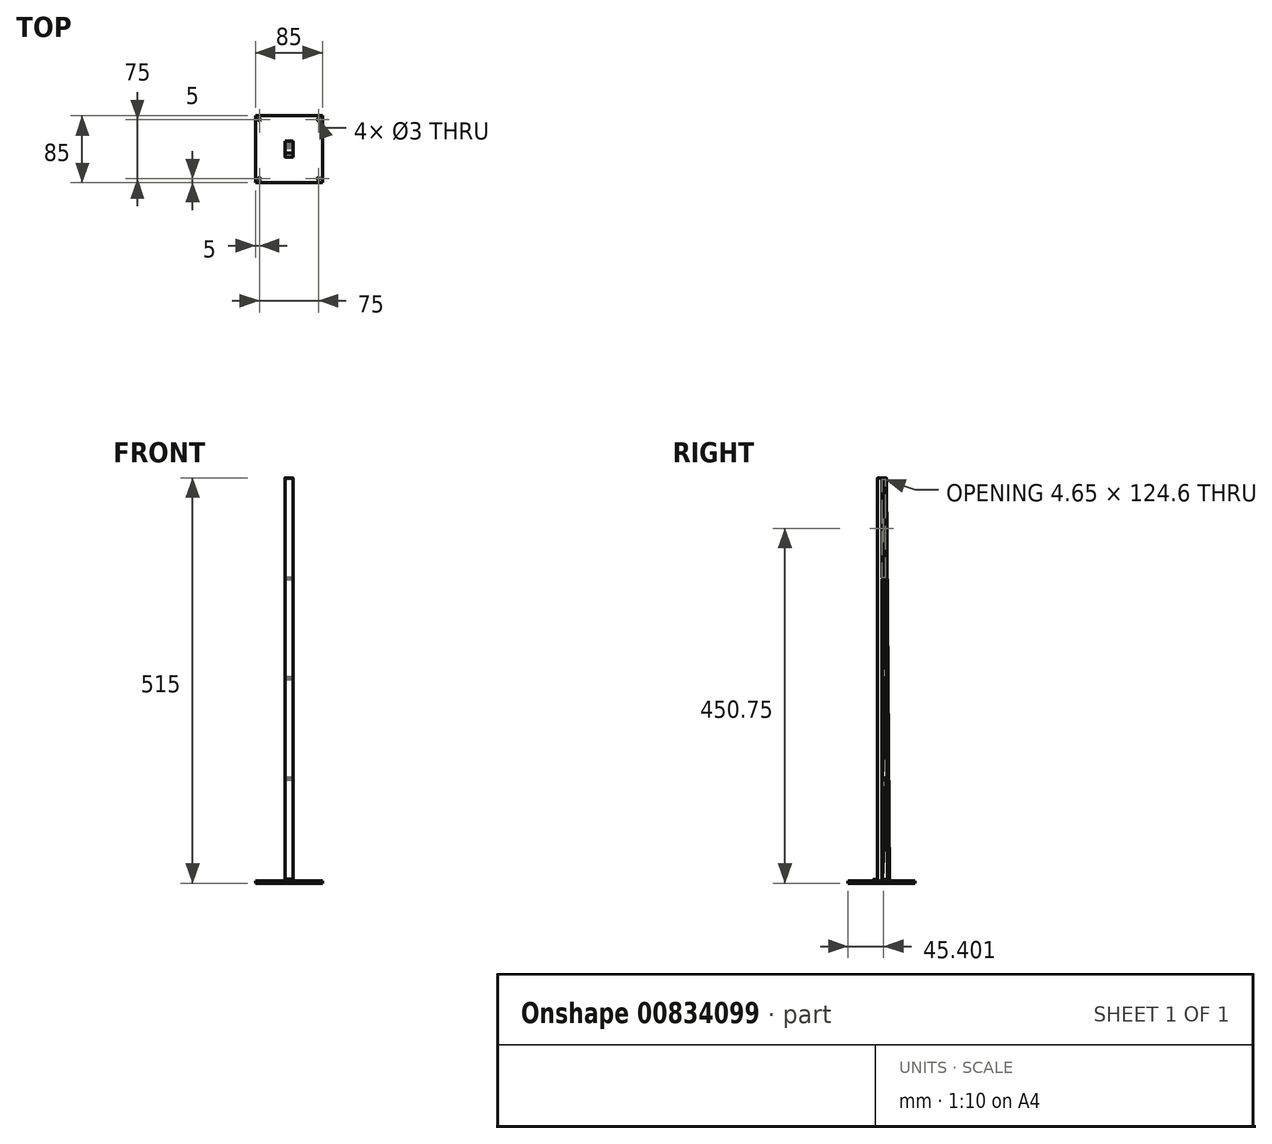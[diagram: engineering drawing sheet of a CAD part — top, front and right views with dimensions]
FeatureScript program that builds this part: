
annotation { "Feature Type Name" : "Feature", "Feature Type Description" : "" }
export const myFeature = defineFeature(function(context is Context, id is Id, definition is map)
    precondition{}
    {
        {
            var Q0;
            Q0=qCreatedBy(makeId("Front.planeOp"),FACE);
            var sketch = newSketch(context, id + "F0", { "sketchPlane" : qUnion([Q0])});
            skLineSegment(sketch, "E0.bottom", {"start": v(5, 255) * mm, "end": v(-5, 255) * mm});
            skLineSegment(sketch, "E0.top", {"start": v(5, -255) * mm, "end": v(-5, -255) * mm});
            skLineSegment(sketch, "E0.left", {"start": v(5, 255) * mm, "end": v(5, -255) * mm});
            skLineSegment(sketch, "E0.right", {"start": v(-5, 255) * mm, "end": v(-5, -255) * mm});
            skPoint(sketch, "E0.middle", {"position": v(0, 0) * mm});
            skSolve(sketch);
        }
        {
            var Q0;
            Q0 = qSketchRegion(id + "F0", true);
            extrude(context, id + "F1", {"entities" : qUnion([Q0]), "depth" : 5 * mm, "offsetDistance" : 25.4 * mm});
        }
        {
            var Q0;
            Q0=makeQuery(id+"F1.opExtrude","SWEPT_FACE",FACE,{"disambiguationData":[OSD([sQuery(id+"F0.wireOp",EDGE,"E0.top")])]});
            var sketch = newSketch(context, id + "F2", { "sketchPlane" : qUnion([Q0])});
            skLineSegment(sketch, "E1.bottom", {"start": v(-5, 10) * mm, "end": v(5, 10) * mm});
            skLineSegment(sketch, "E1.top", {"start": v(-5, -10) * mm, "end": v(5, -10) * mm});
            skLineSegment(sketch, "E1.left", {"start": v(-5, 10) * mm, "end": v(-5, -10) * mm});
            skLineSegment(sketch, "E1.right", {"start": v(5, 10) * mm, "end": v(5, -10) * mm});
            skPoint(sketch, "E1.middle", {"position": v(0, 0) * mm});
            skSolve(sketch);
        }
        {
            var Q0;
            Q0 = qSketchRegion(id + "F2", true);
            extrude(context, id + "F3", {"entities" : qUnion([Q0]), "operationType" : NewBodyOperationType.ADD, "depth" : 2 * mm, "offsetDistance" : 25 * mm});
        }
        {
            var Q0;
            Q0=makeQuery(id+"F1.opExtrude","CAP_FACE",FACE,{"disambiguationData":[OSD([sQuery(id+"F0.wireOp",EDGE,"E0.bottom"),sQuery(id+"F0.wireOp",EDGE,"E0.top"),sQuery(id+"F0.wireOp",EDGE,"E0.left"),sQuery(id+"F0.wireOp",EDGE,"E0.right")])],"isStart":true});
            var sketch = newSketch(context, id + "F4", { "sketchPlane" : qUnion([Q0])});
            skLineSegment(sketch, "E2.bottom", {"start": v(5, -255) * mm, "end": v(-5, -255) * mm});
            skLineSegment(sketch, "E2.top", {"start": v(5, 255) * mm, "end": v(-5, 255) * mm});
            skLineSegment(sketch, "E2.left", {"start": v(5, -255) * mm, "end": v(5, 255) * mm});
            skLineSegment(sketch, "E2.right", {"start": v(-5, -255) * mm, "end": v(-5, 255) * mm});
            skPoint(sketch, "E2.middle", {"position": v(0, 0) * mm});
            skSolve(sketch);
        }
        {
            var Q0;
            Q0=makeQuery(id+"F4.imprint","IMPRINT",FACE,{"disambiguationData":[TD([[makeQuery(id+"F4.imprint","IMPRINT",EDGE,{"derivedFrom":sQuery(id+"F4.wireOp",EDGE,"E2.bottom")}),1.0]])]});
            extrude(context, id + "F5", {"entities" : qUnion([Q0]), "operationType" : NewBodyOperationType.ADD, "depth" : 10 * mm, "offsetDistance" : 25 * mm});
        }
        {
            var Q0;
            Q0=makeQuery(id+"F5.boolean.opBoolean","MERGE",FACE,{"derivedFrom":[makeQuery(id+"F3.boolean.opBoolean","MERGE",FACE,{"derivedFrom":[makeQuery(id+"F1.opExtrude","SWEPT_FACE",FACE,{"disambiguationData":[OSD([sQuery(id+"F0.wireOp",EDGE,"E0.right")])]}),makeQuery(id+"F3.opExtrude","SWEPT_FACE",FACE,{"disambiguationData":[OSD([sQuery(id+"F2.wireOp",EDGE,"E1.left")])]})]}),makeQuery(id+"F5.opExtrude","SWEPT_FACE",FACE,{"disambiguationData":[OSD([sQuery(id+"F4.wireOp",EDGE,"E2.left")])]})]});
            var sketch = newSketch(context, id + "F6", { "sketchPlane" : qUnion([Q0])});
            skLineSegment(sketch, "E3", {"start": v(0, -257) * mm, "end": v(-2.5, 255) * mm});
            skPoint(sketch, "E4", {"position": v(-6.25, 255) * mm});
            skPoint(sketch, "E5", {"position": v(-2.5, 253) * mm});
            skLineSegment(sketch, "E6", {"start": v(-6.25, 255) * mm, "end": v(-10, -257) * mm});
            skSolve(sketch);
        }
        {
            var Q0;
            {var subQ0=sQuery(id+"F6.wireOp",EDGE,"E6");Q0=makeQuery(id+"F6.imprint","IMPRINT",FACE,{"disambiguationData":[TD([[makeQuery(id+"F6.imprint","IMPRINT",EDGE,{"derivedFrom":subQ0}),-1.0]])]});}
            extrude(context, id + "F7", {"entities" : qUnion([Q0]), "operationType" : NewBodyOperationType.REMOVE, "oppositeDirection" : true, "depth" : 25 * mm, "offsetDistance" : 25 * mm});
        }
        {
            var Q0;
            Q0=makeQuery(id+"F5.boolean.opBoolean","MERGE",FACE,{"derivedFrom":[makeQuery(id+"F3.boolean.opBoolean","MERGE",FACE,{"derivedFrom":[makeQuery(id+"F1.opExtrude","SWEPT_FACE",FACE,{"disambiguationData":[OSD([sQuery(id+"F0.wireOp",EDGE,"E0.right")])]}),makeQuery(id+"F3.opExtrude","SWEPT_FACE",FACE,{"disambiguationData":[OSD([sQuery(id+"F2.wireOp",EDGE,"E1.left")])]})]}),makeQuery(id+"F5.opExtrude","SWEPT_FACE",FACE,{"disambiguationData":[OSD([sQuery(id+"F4.wireOp",EDGE,"E2.left")])]})]});
            var sketch = newSketch(context, id + "F8", { "sketchPlane" : qUnion([Q0])});
            skLineSegment(sketch, "E7", {"start": v(-0.62, 255) * mm, "end": v(-0.62, -257) * mm});
            skPoint(sketch, "E8", {"position": v(-0.62, 253) * mm});
            skPoint(sketch, "E9", {"position": v(-0.62, 127.5) * mm});
            skPoint(sketch, "E10", {"position": v(-0.62, 128.5) * mm});
            skPoint(sketch, "E11", {"position": v(-0.62, 126.5) * mm});
            skPoint(sketch, "E12", {"position": v(-0.62, 0) * mm});
            skPoint(sketch, "E13", {"position": v(-0.62, 1) * mm});
            skPoint(sketch, "E14", {"position": v(-0.62, -1) * mm});
            skPoint(sketch, "E15", {"position": v(-0.62, -127.5) * mm});
            skPoint(sketch, "E16", {"position": v(-0.62, -126.5) * mm});
            skPoint(sketch, "E17", {"position": v(-0.62, -128.5) * mm});
            skPoint(sketch, "E18", {"position": v(-0.62, -255) * mm});
            skPoint(sketch, "E19", {"position": v(-7.2, 126.5) * mm});
            skPoint(sketch, "E20", {"position": v(-7.2, 128.5) * mm});
            skPoint(sketch, "E21", {"position": v(-5.2, 126.5) * mm});
            skPoint(sketch, "E22", {"position": v(-5.2, 128.5) * mm});
            skPoint(sketch, "E23", {"position": v(-8.12, -1) * mm});
            skPoint(sketch, "E24", {"position": v(-8.12, 1) * mm});
            skPoint(sketch, "E25", {"position": v(-6.25, 1) * mm});
            skPoint(sketch, "E26", {"position": v(-6.25, -1) * mm});
            skPoint(sketch, "E27", {"position": v(-9.04, -126.5) * mm});
            skPoint(sketch, "E28", {"position": v(-9.04, -128.5) * mm});
            skPoint(sketch, "E29", {"position": v(-7.1, -126.5) * mm});
            skPoint(sketch, "E30", {"position": v(-7.1, -128.5) * mm});
            skPoint(sketch, "E31", {"position": v(-9.99, -255) * mm});
            skPoint(sketch, "E32", {"position": v(-7.99, -255) * mm});
            skPoint(sketch, "E33", {"position": v(-6.25, 253) * mm});
            skPoint(sketch, "E34", {"position": v(-4.25, 253) * mm});
            skLineSegment(sketch, "E35", {"start": v(-0.62, 253) * mm, "end": v(-4.25, 253) * mm});
            skLineSegment(sketch, "E36", {"start": v(-4.25, 253) * mm, "end": v(-5.2, 126.5) * mm});
            skLineSegment(sketch, "E37", {"start": v(-5.2, 126.5) * mm, "end": v(-6.25, -1) * mm});
            skLineSegment(sketch, "E38", {"start": v(-6.25, -1) * mm, "end": v(-7.1, -128.5) * mm});
            skLineSegment(sketch, "E39", {"start": v(-7.1, -128.5) * mm, "end": v(-7.99, -255) * mm});
            skLineSegment(sketch, "E40", {"start": v(-7.99, -255) * mm, "end": v(-0.62, -255) * mm});
            skLineSegment(sketch, "E41", {"start": v(-0.62, 128.5) * mm, "end": v(-5.2, 128.5) * mm});
            skLineSegment(sketch, "E42", {"start": v(-0.62, 126.5) * mm, "end": v(-5.2, 126.5) * mm});
            skLineSegment(sketch, "E43", {"start": v(-0.62, 1) * mm, "end": v(-6.25, 1) * mm});
            skLineSegment(sketch, "E44", {"start": v(-0.62, -1) * mm, "end": v(-6.25, -1) * mm});
            skLineSegment(sketch, "E45", {"start": v(-0.62, -126.5) * mm, "end": v(-7.1, -126.5) * mm});
            skLineSegment(sketch, "E46", {"start": v(-0.62, -128.5) * mm, "end": v(-7.1, -128.5) * mm});
            skPoint(sketch, "E47", {"position": v(-4.2, 126.5) * mm});
            skPoint(sketch, "E48", {"position": v(-5.2, 125.5) * mm});
            skPoint(sketch, "E49", {"position": v(-0.62, 2) * mm});
            skPoint(sketch, "E50", {"position": v(-1.62, 1) * mm});
            skPoint(sketch, "E51", {"position": v(-0.62, -125.5) * mm});
            skPoint(sketch, "E52", {"position": v(-1.62, -126.5) * mm});
            skPoint(sketch, "E53", {"position": v(-0.62, -254) * mm});
            skPoint(sketch, "E54", {"position": v(-1.62, -255) * mm});
            skPoint(sketch, "E55", {"position": v(-6.1, -128.5) * mm});
            skPoint(sketch, "E56", {"position": v(-7.1, -129.5) * mm});
            skPoint(sketch, "E57", {"position": v(-5.25, -1) * mm});
            skPoint(sketch, "E58", {"position": v(-6.26, -2) * mm});
            skLineSegment(sketch, "E59", {"start": v(-4.2, 126.5) * mm, "end": v(-0.62, 2) * mm});
            skLineSegment(sketch, "E60", {"start": v(-1.62, 1) * mm, "end": v(-5.2, 125.5) * mm});
            skLineSegment(sketch, "E61", {"start": v(-5.25, -1) * mm, "end": v(-0.62, -125.5) * mm});
            skLineSegment(sketch, "E62", {"start": v(-6.26, -2) * mm, "end": v(-1.62, -126.5) * mm});
            skLineSegment(sketch, "E63", {"start": v(-6.1, -128.5) * mm, "end": v(-0.62, -254) * mm});
            skLineSegment(sketch, "E64", {"start": v(-1.62, -255) * mm, "end": v(-7.1, -129.5) * mm});
            skSolve(sketch);
        }
        {
            var Q0;
            {var subQ3=sQuery(id+"F8.wireOp",EDGE,"E63");Q0=makeQuery(id+"F8.imprint","IMPRINT",FACE,{"disambiguationData":[TD([[makeQuery(id+"F8.imprint","IMPRINT",EDGE,{"derivedFrom":subQ3}),1.0]])]});}
            var Q1;
            {var subQ3=sQuery(id+"F8.wireOp",EDGE,"E64");Q1=makeQuery(id+"F8.imprint","IMPRINT",FACE,{"disambiguationData":[TD([[makeQuery(id+"F8.imprint","IMPRINT",EDGE,{"derivedFrom":subQ3}),1.0]])]});}
            var Q2;
            {var subQ0=sQuery(id+"F8.wireOp",EDGE,"E62");Q2=makeQuery(id+"F8.imprint","IMPRINT",FACE,{"disambiguationData":[TD([[makeQuery(id+"F8.imprint","IMPRINT",EDGE,{"derivedFrom":subQ0}),-1.0]])]});}
            var Q3;
            {var subQ3=sQuery(id+"F8.wireOp",EDGE,"E61");Q3=makeQuery(id+"F8.imprint","IMPRINT",FACE,{"disambiguationData":[TD([[makeQuery(id+"F8.imprint","IMPRINT",EDGE,{"derivedFrom":subQ3}),1.0]])]});}
            var Q4;
            {var subQ0=sQuery(id+"F8.wireOp",EDGE,"E60");Q4=makeQuery(id+"F8.imprint","IMPRINT",FACE,{"disambiguationData":[TD([[makeQuery(id+"F8.imprint","IMPRINT",EDGE,{"derivedFrom":subQ0}),1.0]])]});}
            var Q5;
            {var subQ3=sQuery(id+"F8.wireOp",EDGE,"E59");Q5=makeQuery(id+"F8.imprint","IMPRINT",FACE,{"disambiguationData":[TD([[makeQuery(id+"F8.imprint","IMPRINT",EDGE,{"derivedFrom":subQ3}),1.0]])]});}
            var Q6;
            {var subQ0=sQuery(id+"F8.wireOp",EDGE,"E35");Q6=makeQuery(id+"F8.imprint","IMPRINT",FACE,{"disambiguationData":[TD([[makeQuery(id+"F8.imprint","IMPRINT",EDGE,{"derivedFrom":subQ0}),1.0]])]});}
            extrude(context, id + "F9", {"entities" : qUnion([Q0, Q1, Q2, Q3, Q4, Q5, Q6]), "operationType" : NewBodyOperationType.REMOVE, "oppositeDirection" : true, "depth" : 25 * mm, "offsetDistance" : 25 * mm});
        }
        {
            var Q0;
            {var subQ0=sQuery(id+"F2.wireOp",EDGE,"E1.bottom");var subQ2=sQuery(id+"F2.wireOp",EDGE,"E1.left");var subQ4=sQuery(id+"F2.wireOp",EDGE,"E1.right");Q0=makeQuery(id+"F3.boolean.opBoolean","SPLIT",FACE,{"disambiguationData":[TD([makeQuery(id+"F3.opExtrude","SWEPT_FACE",FACE,{"disambiguationData":[OSD([subQ0])]})])],"derivedFrom":makeQuery(id+"F3.opExtrude","CAP_FACE",FACE,{"disambiguationData":[OSD([subQ0,sQuery(id+"F2.wireOp",EDGE,"E1.top"),subQ2,subQ4])],"isStart":true})});}
            var Q1;
            Q1=makeQuery(id+"F3.opExtrude","CAP_EDGE",EDGE,{"disambiguationData":[OSD([sQuery(id+"F2.wireOp",EDGE,"E1.right")])],"isStart":false});
            var Q2;
            {var subQ0=sQuery(id+"F2.wireOp",EDGE,"E1.top");Q2=makeQuery(id+"F7.boolean.opBoolean","MERGE",EDGE,{"derivedFrom":[makeQuery(id+"F3.opExtrude","CAP_EDGE",EDGE,{"disambiguationData":[OSD([subQ0])],"isStart":false}),makeQuery(id+"F7.opExtrude","SWEPT_EDGE",EDGE,{"disambiguationData":[OSD([subQ0,sQuery(id+"F2.wireOp",EDGE,"E1.left"),sQuery(id+"F4.wireOp",EDGE,"E2.left"),sQuery(id+"F6.wireOp",EDGE,"E6")])]})]});}
            var Q3;
            Q3=makeQuery(id+"F3.opExtrude","CAP_EDGE",EDGE,{"disambiguationData":[OSD([sQuery(id+"F2.wireOp",EDGE,"E1.left")])],"isStart":false});
            var Q4;
            Q4=makeQuery(id+"F3.opExtrude","CAP_EDGE",EDGE,{"disambiguationData":[OSD([sQuery(id+"F2.wireOp",EDGE,"E1.bottom")])],"isStart":false});
            fillet(context, id + "F10", {"entities" : qUnion([Q0, Q1, Q2, Q3, Q4]), "radius" : 0.05 * mm, "tangentPropagation" : true, "allowEdgeOverflow" : false});
        }
        {
            var Q0;
            {var subQ0=sQuery(id+"F8.wireOp",EDGE,"E7");Q0=makeQuery(id+"F9.boolean.opBoolean","COPY",EDGE,{"derivedFrom":makeQuery(id+"F9.opExtrude","CAP_EDGE",EDGE,{"disambiguationData":[OSD([subQ0]),TDD([makeQuery(id+"F8.imprint","IMPRINT",EDGE,{"disambiguationData":[TD([[makeQuery(id+"F8.imprint","INTERSECT",VERTEX,{"derivedFrom":[subQ0,sQuery(id+"F8.wireOp",EDGE,"E35")]}),-1.0]])],"derivedFrom":subQ0})])],"isStart":true})});}
            var Q1;
            Q1=makeQuery(id+"F9.boolean.opBoolean","COPY",EDGE,{"derivedFrom":makeQuery(id+"F9.opExtrude","CAP_EDGE",EDGE,{"disambiguationData":[OSD([sQuery(id+"F8.wireOp",EDGE,"E36")])],"isStart":true})});
            var Q2;
            Q2=makeQuery(id+"F9.boolean.opBoolean","COPY",EDGE,{"derivedFrom":makeQuery(id+"F9.opExtrude","CAP_EDGE",EDGE,{"disambiguationData":[OSD([sQuery(id+"F8.wireOp",EDGE,"E35")])],"isStart":true})});
            var Q3;
            Q3=makeQuery(id+"F9.boolean.opBoolean","COPY",EDGE,{"derivedFrom":makeQuery(id+"F9.opExtrude","CAP_EDGE",EDGE,{"disambiguationData":[OSD([sQuery(id+"F8.wireOp",EDGE,"E41")])],"isStart":true})});
            var Q4;
            Q4=makeQuery(id+"F9.boolean.opBoolean","COPY",EDGE,{"derivedFrom":makeQuery(id+"F9.opExtrude","CAP_EDGE",EDGE,{"disambiguationData":[OSD([sQuery(id+"F8.wireOp",EDGE,"E42")])],"isStart":true})});
            var Q5;
            Q5=makeQuery(id+"F9.boolean.opBoolean","COPY",EDGE,{"derivedFrom":makeQuery(id+"F9.opExtrude","CAP_EDGE",EDGE,{"disambiguationData":[OSD([sQuery(id+"F8.wireOp",EDGE,"E59")])],"isStart":true})});
            var Q6;
            {var subQ0=sQuery(id+"F8.wireOp",EDGE,"E7");Q6=makeQuery(id+"F9.boolean.opBoolean","COPY",EDGE,{"derivedFrom":makeQuery(id+"F9.opExtrude","CAP_EDGE",EDGE,{"disambiguationData":[OSD([subQ0]),TDD([makeQuery(id+"F8.imprint","IMPRINT",EDGE,{"disambiguationData":[TD([[makeQuery(id+"F8.imprint","INTERSECT",VERTEX,{"derivedFrom":[subQ0,sQuery(id+"F8.wireOp",EDGE,"E42")]}),-1.0]])],"derivedFrom":subQ0})])],"isStart":true})});}
            var Q7;
            Q7=makeQuery(id+"F9.boolean.opBoolean","COPY",EDGE,{"derivedFrom":makeQuery(id+"F9.opExtrude","CAP_EDGE",EDGE,{"disambiguationData":[OSD([sQuery(id+"F8.wireOp",EDGE,"E37")])],"isStart":true})});
            var Q8;
            Q8=makeQuery(id+"F9.boolean.opBoolean","COPY",EDGE,{"derivedFrom":makeQuery(id+"F9.opExtrude","CAP_EDGE",EDGE,{"disambiguationData":[OSD([sQuery(id+"F8.wireOp",EDGE,"E60")])],"isStart":true})});
            var Q9;
            Q9=makeQuery(id+"F9.boolean.opBoolean","COPY",EDGE,{"derivedFrom":makeQuery(id+"F9.opExtrude","CAP_EDGE",EDGE,{"disambiguationData":[OSD([sQuery(id+"F8.wireOp",EDGE,"E43")])],"isStart":true})});
            var Q10;
            Q10=makeQuery(id+"F9.boolean.opBoolean","COPY",EDGE,{"derivedFrom":makeQuery(id+"F9.opExtrude","CAP_EDGE",EDGE,{"disambiguationData":[OSD([sQuery(id+"F8.wireOp",EDGE,"E61")])],"isStart":true})});
            var Q11;
            Q11=makeQuery(id+"F9.boolean.opBoolean","COPY",EDGE,{"derivedFrom":makeQuery(id+"F9.opExtrude","CAP_EDGE",EDGE,{"disambiguationData":[OSD([sQuery(id+"F8.wireOp",EDGE,"E44")])],"isStart":true})});
            var Q12;
            {var subQ0=sQuery(id+"F8.wireOp",EDGE,"E7");Q12=makeQuery(id+"F9.boolean.opBoolean","COPY",EDGE,{"derivedFrom":makeQuery(id+"F9.opExtrude","CAP_EDGE",EDGE,{"disambiguationData":[OSD([subQ0]),TDD([makeQuery(id+"F8.imprint","IMPRINT",EDGE,{"disambiguationData":[TD([[makeQuery(id+"F8.imprint","INTERSECT",VERTEX,{"derivedFrom":[subQ0,sQuery(id+"F8.wireOp",EDGE,"E44")]}),-1.0]])],"derivedFrom":subQ0})])],"isStart":true})});}
            var Q13;
            Q13=makeQuery(id+"F9.boolean.opBoolean","COPY",EDGE,{"derivedFrom":makeQuery(id+"F9.opExtrude","CAP_EDGE",EDGE,{"disambiguationData":[OSD([sQuery(id+"F8.wireOp",EDGE,"E38")])],"isStart":true})});
            var Q14;
            Q14=makeQuery(id+"F9.boolean.opBoolean","COPY",EDGE,{"derivedFrom":makeQuery(id+"F9.opExtrude","CAP_EDGE",EDGE,{"disambiguationData":[OSD([sQuery(id+"F8.wireOp",EDGE,"E62")])],"isStart":true})});
            var Q15;
            Q15=makeQuery(id+"F9.boolean.opBoolean","COPY",EDGE,{"derivedFrom":makeQuery(id+"F9.opExtrude","CAP_EDGE",EDGE,{"disambiguationData":[OSD([sQuery(id+"F8.wireOp",EDGE,"E45")])],"isStart":true})});
            var Q16;
            Q16=makeQuery(id+"F9.boolean.opBoolean","COPY",EDGE,{"derivedFrom":makeQuery(id+"F9.opExtrude","CAP_EDGE",EDGE,{"disambiguationData":[OSD([sQuery(id+"F8.wireOp",EDGE,"E46")])],"isStart":true})});
            var Q17;
            Q17=makeQuery(id+"F9.boolean.opBoolean","COPY",EDGE,{"derivedFrom":makeQuery(id+"F9.opExtrude","CAP_EDGE",EDGE,{"disambiguationData":[OSD([sQuery(id+"F8.wireOp",EDGE,"E63")])],"isStart":true})});
            var Q18;
            {var subQ0=sQuery(id+"F8.wireOp",EDGE,"E7");Q18=makeQuery(id+"F9.boolean.opBoolean","COPY",EDGE,{"derivedFrom":makeQuery(id+"F9.opExtrude","CAP_EDGE",EDGE,{"disambiguationData":[OSD([subQ0]),TDD([makeQuery(id+"F8.imprint","IMPRINT",EDGE,{"disambiguationData":[TD([[makeQuery(id+"F8.imprint","INTERSECT",VERTEX,{"derivedFrom":[subQ0,sQuery(id+"F8.wireOp",EDGE,"E46")]}),-1.0]])],"derivedFrom":subQ0})])],"isStart":true})});}
            var Q19;
            Q19=makeQuery(id+"F9.boolean.opBoolean","COPY",EDGE,{"derivedFrom":makeQuery(id+"F9.opExtrude","CAP_EDGE",EDGE,{"disambiguationData":[OSD([sQuery(id+"F8.wireOp",EDGE,"E64")])],"isStart":true})});
            var Q20;
            Q20=makeQuery(id+"F9.boolean.opBoolean","COPY",EDGE,{"derivedFrom":makeQuery(id+"F9.opExtrude","CAP_EDGE",EDGE,{"disambiguationData":[OSD([sQuery(id+"F8.wireOp",EDGE,"E39")])],"isStart":true})});
            var Q21;
            Q21=makeQuery(id+"F9.boolean.opBoolean","COPY",EDGE,{"derivedFrom":makeQuery(id+"F9.opExtrude","CAP_EDGE",EDGE,{"disambiguationData":[OSD([sQuery(id+"F8.wireOp",EDGE,"E40")])],"isStart":true})});
            var Q22;
            {var subQ0=sQuery(id+"F2.wireOp",EDGE,"E1.left");var subQ1=makeQuery(id+"F3.opExtrude","SWEPT_FACE",FACE,{"disambiguationData":[OSD([subQ0])]});var subQ2=sQuery(id+"F0.wireOp",EDGE,"E0.right");var subQ3=makeQuery(id+"F1.opExtrude","SWEPT_FACE",FACE,{"disambiguationData":[OSD([subQ2])]});var subQ4=sQuery(id+"F2.wireOp",EDGE,"E1.bottom");Q22=makeQuery(id+"F10.opFillet","BLEND_EDGE",EDGE,{"blendedFrom":[makeQuery(id+"F3.boolean.opBoolean","SPLIT",EDGE,{"disambiguationData":[TD([makeQuery(id+"F3.opExtrude","SWEPT_FACE",FACE,{"disambiguationData":[OSD([subQ4])]})])],"derivedFrom":makeQuery(id+"F3.opExtrude","CAP_EDGE",EDGE,{"disambiguationData":[OSD([subQ0])],"isStart":true})}),makeQuery(id+"F5.boolean.opBoolean","MERGE",FACE,{"derivedFrom":[makeQuery(id+"F3.boolean.opBoolean","MERGE",FACE,{"derivedFrom":[subQ3,subQ1]}),makeQuery(id+"F5.opExtrude","SWEPT_FACE",FACE,{"disambiguationData":[OSD([sQuery(id+"F4.wireOp",EDGE,"E2.left")])]})]})],"blendedInto":[makeQuery(id+"F5.boolean.opBoolean","MERGE",FACE,{"derivedFrom":[makeQuery(id+"F3.boolean.opBoolean","MERGE",FACE,{"derivedFrom":[subQ3,subQ1]}),makeQuery(id+"F5.opExtrude","SWEPT_FACE",FACE,{"disambiguationData":[OSD([sQuery(id+"F4.wireOp",EDGE,"E2.left")])]})]})]});}
            var Q23;
            {var subQ0=sQuery(id+"F0.wireOp",EDGE,"E0.right");Q23=makeQuery(id+"F10.opFillet","BLEND_EDGE",EDGE,{"blendedFrom":[makeQuery(id+"F1.opExtrude","CAP_EDGE",EDGE,{"disambiguationData":[OSD([subQ0])],"isStart":false}),makeQuery(id+"F5.boolean.opBoolean","MERGE",FACE,{"derivedFrom":[makeQuery(id+"F3.boolean.opBoolean","MERGE",FACE,{"derivedFrom":[makeQuery(id+"F1.opExtrude","SWEPT_FACE",FACE,{"disambiguationData":[OSD([subQ0])]}),makeQuery(id+"F3.opExtrude","SWEPT_FACE",FACE,{"disambiguationData":[OSD([sQuery(id+"F2.wireOp",EDGE,"E1.left")])]})]}),makeQuery(id+"F5.opExtrude","SWEPT_FACE",FACE,{"disambiguationData":[OSD([sQuery(id+"F4.wireOp",EDGE,"E2.left")])]})]})],"blendedInto":[makeQuery(id+"F5.boolean.opBoolean","MERGE",FACE,{"derivedFrom":[makeQuery(id+"F3.boolean.opBoolean","MERGE",FACE,{"derivedFrom":[makeQuery(id+"F1.opExtrude","SWEPT_FACE",FACE,{"disambiguationData":[OSD([subQ0])]}),makeQuery(id+"F3.opExtrude","SWEPT_FACE",FACE,{"disambiguationData":[OSD([sQuery(id+"F2.wireOp",EDGE,"E1.left")])]})]}),makeQuery(id+"F5.opExtrude","SWEPT_FACE",FACE,{"disambiguationData":[OSD([sQuery(id+"F4.wireOp",EDGE,"E2.left")])]})]})]});}
            var Q24;
            {var subQ0=sQuery(id+"F2.wireOp",EDGE,"E1.left");Q24=makeQuery(id+"F10.opFillet","BLEND_EDGE",EDGE,{"blendedFrom":[makeQuery(id+"F3.opExtrude","CAP_EDGE",EDGE,{"disambiguationData":[OSD([subQ0])],"isStart":false}),makeQuery(id+"F5.boolean.opBoolean","MERGE",FACE,{"derivedFrom":[makeQuery(id+"F3.boolean.opBoolean","MERGE",FACE,{"derivedFrom":[makeQuery(id+"F1.opExtrude","SWEPT_FACE",FACE,{"disambiguationData":[OSD([sQuery(id+"F0.wireOp",EDGE,"E0.right")])]}),makeQuery(id+"F3.opExtrude","SWEPT_FACE",FACE,{"disambiguationData":[OSD([subQ0])]})]}),makeQuery(id+"F5.opExtrude","SWEPT_FACE",FACE,{"disambiguationData":[OSD([sQuery(id+"F4.wireOp",EDGE,"E2.left")])]})]})],"blendedInto":[makeQuery(id+"F5.boolean.opBoolean","MERGE",FACE,{"derivedFrom":[makeQuery(id+"F3.boolean.opBoolean","MERGE",FACE,{"derivedFrom":[makeQuery(id+"F1.opExtrude","SWEPT_FACE",FACE,{"disambiguationData":[OSD([sQuery(id+"F0.wireOp",EDGE,"E0.right")])]}),makeQuery(id+"F3.opExtrude","SWEPT_FACE",FACE,{"disambiguationData":[OSD([subQ0])]})]}),makeQuery(id+"F5.opExtrude","SWEPT_FACE",FACE,{"disambiguationData":[OSD([sQuery(id+"F4.wireOp",EDGE,"E2.left")])]})]})]});}
            var Q25;
            Q25=makeQuery(id+"F3.opExtrude","SWEPT_EDGE",EDGE,{"disambiguationData":[OSD([sQuery(id+"F2.wireOp",EDGE,"E1.bottom"),sQuery(id+"F2.wireOp",EDGE,"E1.left")])]});
            var Q26;
            Q26=makeQuery(id+"F7.boolean.opBoolean","COPY",EDGE,{"derivedFrom":makeQuery(id+"F7.opExtrude","CAP_EDGE",EDGE,{"disambiguationData":[OSD([sQuery(id+"F6.wireOp",EDGE,"E6")])],"isStart":true})});
            fillet(context, id + "F11", {"entities" : qUnion([Q0, Q1, Q2, Q3, Q4, Q5, Q6, Q7, Q8, Q9, Q10, Q11, Q12, Q13, Q14, Q15, Q16, Q17, Q18, Q19, Q20, Q21, Q22, Q23, Q24, Q25, Q26]), "radius" : 0.05 * mm, "tangentPropagation" : true, "allowEdgeOverflow" : false});
        }
        {
            var Q0;
            Q0=makeQuery(id+"F5.boolean.opBoolean","MERGE",EDGE,{"derivedFrom":[makeQuery(id+"F1.opExtrude","SWEPT_EDGE",EDGE,{"disambiguationData":[OSD([sQuery(id+"F0.wireOp",EDGE,"E0.bottom"),sQuery(id+"F0.wireOp",EDGE,"E0.left")])]}),makeQuery(id+"F5.opExtrude","SWEPT_EDGE",EDGE,{"disambiguationData":[OSD([sQuery(id+"F4.wireOp",EDGE,"E2.top"),sQuery(id+"F4.wireOp",EDGE,"E2.right")])]})]});
            var Q1;
            {var subQ0=sQuery(id+"F0.wireOp",EDGE,"E0.left");Q1=makeQuery(id+"F10.opFillet","BLEND_EDGE",EDGE,{"blendedFrom":[makeQuery(id+"F1.opExtrude","CAP_EDGE",EDGE,{"disambiguationData":[OSD([subQ0])],"isStart":false}),makeQuery(id+"F1.opExtrude","CAP_FACE",FACE,{"disambiguationData":[OSD([sQuery(id+"F0.wireOp",EDGE,"E0.bottom"),sQuery(id+"F0.wireOp",EDGE,"E0.top"),subQ0,sQuery(id+"F0.wireOp",EDGE,"E0.right")])],"isStart":false})],"blendedInto":[makeQuery(id+"F1.opExtrude","CAP_FACE",FACE,{"disambiguationData":[OSD([sQuery(id+"F0.wireOp",EDGE,"E0.bottom"),sQuery(id+"F0.wireOp",EDGE,"E0.top"),subQ0,sQuery(id+"F0.wireOp",EDGE,"E0.right")])],"isStart":false})]});}
            var Q2;
            Q2=makeQuery(id+"F7.boolean.opBoolean","INTERSECT",EDGE,{"derivedFrom":[makeQuery(id+"F5.boolean.opBoolean","MERGE",FACE,{"derivedFrom":[makeQuery(id+"F3.boolean.opBoolean","MERGE",FACE,{"derivedFrom":[makeQuery(id+"F1.opExtrude","SWEPT_FACE",FACE,{"disambiguationData":[OSD([sQuery(id+"F0.wireOp",EDGE,"E0.left")])]}),makeQuery(id+"F3.opExtrude","SWEPT_FACE",FACE,{"disambiguationData":[OSD([sQuery(id+"F2.wireOp",EDGE,"E1.right")])]})]}),makeQuery(id+"F5.opExtrude","SWEPT_FACE",FACE,{"disambiguationData":[OSD([sQuery(id+"F4.wireOp",EDGE,"E2.right")])]})]}),makeQuery(id+"F7.opExtrude","SWEPT_FACE",FACE,{"disambiguationData":[OSD([sQuery(id+"F6.wireOp",EDGE,"E6")])]})]});
            var Q3;
            Q3=makeQuery(id+"F9.boolean.opBoolean","INTERSECT",EDGE,{"derivedFrom":[makeQuery(id+"F5.boolean.opBoolean","MERGE",FACE,{"derivedFrom":[makeQuery(id+"F3.boolean.opBoolean","MERGE",FACE,{"derivedFrom":[makeQuery(id+"F1.opExtrude","SWEPT_FACE",FACE,{"disambiguationData":[OSD([sQuery(id+"F0.wireOp",EDGE,"E0.left")])]}),makeQuery(id+"F3.opExtrude","SWEPT_FACE",FACE,{"disambiguationData":[OSD([sQuery(id+"F2.wireOp",EDGE,"E1.right")])]})]}),makeQuery(id+"F5.opExtrude","SWEPT_FACE",FACE,{"disambiguationData":[OSD([sQuery(id+"F4.wireOp",EDGE,"E2.right")])]})]}),makeQuery(id+"F9.opExtrude","SWEPT_FACE",FACE,{"disambiguationData":[OSD([sQuery(id+"F8.wireOp",EDGE,"E36")])]})]});
            var Q4;
            Q4=makeQuery(id+"F9.boolean.opBoolean","INTERSECT",EDGE,{"derivedFrom":[makeQuery(id+"F5.boolean.opBoolean","MERGE",FACE,{"derivedFrom":[makeQuery(id+"F3.boolean.opBoolean","MERGE",FACE,{"derivedFrom":[makeQuery(id+"F1.opExtrude","SWEPT_FACE",FACE,{"disambiguationData":[OSD([sQuery(id+"F0.wireOp",EDGE,"E0.left")])]}),makeQuery(id+"F3.opExtrude","SWEPT_FACE",FACE,{"disambiguationData":[OSD([sQuery(id+"F2.wireOp",EDGE,"E1.right")])]})]}),makeQuery(id+"F5.opExtrude","SWEPT_FACE",FACE,{"disambiguationData":[OSD([sQuery(id+"F4.wireOp",EDGE,"E2.right")])]})]}),makeQuery(id+"F9.opExtrude","SWEPT_FACE",FACE,{"disambiguationData":[OSD([sQuery(id+"F8.wireOp",EDGE,"E35")])]})]});
            var Q5;
            {var subQ0=sQuery(id+"F8.wireOp",EDGE,"E7");Q5=makeQuery(id+"F9.boolean.opBoolean","INTERSECT",EDGE,{"derivedFrom":[makeQuery(id+"F5.boolean.opBoolean","MERGE",FACE,{"derivedFrom":[makeQuery(id+"F3.boolean.opBoolean","MERGE",FACE,{"derivedFrom":[makeQuery(id+"F1.opExtrude","SWEPT_FACE",FACE,{"disambiguationData":[OSD([sQuery(id+"F0.wireOp",EDGE,"E0.left")])]}),makeQuery(id+"F3.opExtrude","SWEPT_FACE",FACE,{"disambiguationData":[OSD([sQuery(id+"F2.wireOp",EDGE,"E1.right")])]})]}),makeQuery(id+"F5.opExtrude","SWEPT_FACE",FACE,{"disambiguationData":[OSD([sQuery(id+"F4.wireOp",EDGE,"E2.right")])]})]}),makeQuery(id+"F9.opExtrude","SWEPT_FACE",FACE,{"disambiguationData":[OSD([subQ0]),TDD([makeQuery(id+"F8.imprint","IMPRINT",EDGE,{"disambiguationData":[TD([[makeQuery(id+"F8.imprint","INTERSECT",VERTEX,{"derivedFrom":[subQ0,sQuery(id+"F8.wireOp",EDGE,"E35")]}),-1.0]])],"derivedFrom":subQ0})])]})]});}
            var Q6;
            Q6=makeQuery(id+"F9.boolean.opBoolean","INTERSECT",EDGE,{"derivedFrom":[makeQuery(id+"F5.boolean.opBoolean","MERGE",FACE,{"derivedFrom":[makeQuery(id+"F3.boolean.opBoolean","MERGE",FACE,{"derivedFrom":[makeQuery(id+"F1.opExtrude","SWEPT_FACE",FACE,{"disambiguationData":[OSD([sQuery(id+"F0.wireOp",EDGE,"E0.left")])]}),makeQuery(id+"F3.opExtrude","SWEPT_FACE",FACE,{"disambiguationData":[OSD([sQuery(id+"F2.wireOp",EDGE,"E1.right")])]})]}),makeQuery(id+"F5.opExtrude","SWEPT_FACE",FACE,{"disambiguationData":[OSD([sQuery(id+"F4.wireOp",EDGE,"E2.right")])]})]}),makeQuery(id+"F9.opExtrude","SWEPT_FACE",FACE,{"disambiguationData":[OSD([sQuery(id+"F8.wireOp",EDGE,"E42")])]})]});
            var Q7;
            {var subQ0=sQuery(id+"F8.wireOp",EDGE,"E7");Q7=makeQuery(id+"F9.boolean.opBoolean","INTERSECT",EDGE,{"derivedFrom":[makeQuery(id+"F5.boolean.opBoolean","MERGE",FACE,{"derivedFrom":[makeQuery(id+"F3.boolean.opBoolean","MERGE",FACE,{"derivedFrom":[makeQuery(id+"F1.opExtrude","SWEPT_FACE",FACE,{"disambiguationData":[OSD([sQuery(id+"F0.wireOp",EDGE,"E0.left")])]}),makeQuery(id+"F3.opExtrude","SWEPT_FACE",FACE,{"disambiguationData":[OSD([sQuery(id+"F2.wireOp",EDGE,"E1.right")])]})]}),makeQuery(id+"F5.opExtrude","SWEPT_FACE",FACE,{"disambiguationData":[OSD([sQuery(id+"F4.wireOp",EDGE,"E2.right")])]})]}),makeQuery(id+"F9.opExtrude","SWEPT_FACE",FACE,{"disambiguationData":[OSD([subQ0]),TDD([makeQuery(id+"F8.imprint","IMPRINT",EDGE,{"disambiguationData":[TD([[makeQuery(id+"F8.imprint","INTERSECT",VERTEX,{"derivedFrom":[subQ0,sQuery(id+"F8.wireOp",EDGE,"E42")]}),-1.0]])],"derivedFrom":subQ0})])]})]});}
            var Q8;
            Q8=makeQuery(id+"F9.boolean.opBoolean","INTERSECT",EDGE,{"derivedFrom":[makeQuery(id+"F5.boolean.opBoolean","MERGE",FACE,{"derivedFrom":[makeQuery(id+"F3.boolean.opBoolean","MERGE",FACE,{"derivedFrom":[makeQuery(id+"F1.opExtrude","SWEPT_FACE",FACE,{"disambiguationData":[OSD([sQuery(id+"F0.wireOp",EDGE,"E0.left")])]}),makeQuery(id+"F3.opExtrude","SWEPT_FACE",FACE,{"disambiguationData":[OSD([sQuery(id+"F2.wireOp",EDGE,"E1.right")])]})]}),makeQuery(id+"F5.opExtrude","SWEPT_FACE",FACE,{"disambiguationData":[OSD([sQuery(id+"F4.wireOp",EDGE,"E2.right")])]})]}),makeQuery(id+"F9.opExtrude","SWEPT_FACE",FACE,{"disambiguationData":[OSD([sQuery(id+"F8.wireOp",EDGE,"E59")])]})]});
            var Q9;
            Q9=makeQuery(id+"F9.boolean.opBoolean","INTERSECT",EDGE,{"derivedFrom":[makeQuery(id+"F5.boolean.opBoolean","MERGE",FACE,{"derivedFrom":[makeQuery(id+"F3.boolean.opBoolean","MERGE",FACE,{"derivedFrom":[makeQuery(id+"F1.opExtrude","SWEPT_FACE",FACE,{"disambiguationData":[OSD([sQuery(id+"F0.wireOp",EDGE,"E0.left")])]}),makeQuery(id+"F3.opExtrude","SWEPT_FACE",FACE,{"disambiguationData":[OSD([sQuery(id+"F2.wireOp",EDGE,"E1.right")])]})]}),makeQuery(id+"F5.opExtrude","SWEPT_FACE",FACE,{"disambiguationData":[OSD([sQuery(id+"F4.wireOp",EDGE,"E2.right")])]})]}),makeQuery(id+"F9.opExtrude","SWEPT_FACE",FACE,{"disambiguationData":[OSD([sQuery(id+"F8.wireOp",EDGE,"E37")])]})]});
            var Q10;
            Q10=makeQuery(id+"F9.boolean.opBoolean","INTERSECT",EDGE,{"derivedFrom":[makeQuery(id+"F5.boolean.opBoolean","MERGE",FACE,{"derivedFrom":[makeQuery(id+"F3.boolean.opBoolean","MERGE",FACE,{"derivedFrom":[makeQuery(id+"F1.opExtrude","SWEPT_FACE",FACE,{"disambiguationData":[OSD([sQuery(id+"F0.wireOp",EDGE,"E0.left")])]}),makeQuery(id+"F3.opExtrude","SWEPT_FACE",FACE,{"disambiguationData":[OSD([sQuery(id+"F2.wireOp",EDGE,"E1.right")])]})]}),makeQuery(id+"F5.opExtrude","SWEPT_FACE",FACE,{"disambiguationData":[OSD([sQuery(id+"F4.wireOp",EDGE,"E2.right")])]})]}),makeQuery(id+"F9.opExtrude","SWEPT_FACE",FACE,{"disambiguationData":[OSD([sQuery(id+"F8.wireOp",EDGE,"E60")])]})]});
            var Q11;
            Q11=makeQuery(id+"F9.boolean.opBoolean","INTERSECT",EDGE,{"derivedFrom":[makeQuery(id+"F5.boolean.opBoolean","MERGE",FACE,{"derivedFrom":[makeQuery(id+"F3.boolean.opBoolean","MERGE",FACE,{"derivedFrom":[makeQuery(id+"F1.opExtrude","SWEPT_FACE",FACE,{"disambiguationData":[OSD([sQuery(id+"F0.wireOp",EDGE,"E0.left")])]}),makeQuery(id+"F3.opExtrude","SWEPT_FACE",FACE,{"disambiguationData":[OSD([sQuery(id+"F2.wireOp",EDGE,"E1.right")])]})]}),makeQuery(id+"F5.opExtrude","SWEPT_FACE",FACE,{"disambiguationData":[OSD([sQuery(id+"F4.wireOp",EDGE,"E2.right")])]})]}),makeQuery(id+"F9.opExtrude","SWEPT_FACE",FACE,{"disambiguationData":[OSD([sQuery(id+"F8.wireOp",EDGE,"E43")])]})]});
            var Q12;
            Q12=makeQuery(id+"F9.boolean.opBoolean","INTERSECT",EDGE,{"derivedFrom":[makeQuery(id+"F5.boolean.opBoolean","MERGE",FACE,{"derivedFrom":[makeQuery(id+"F3.boolean.opBoolean","MERGE",FACE,{"derivedFrom":[makeQuery(id+"F1.opExtrude","SWEPT_FACE",FACE,{"disambiguationData":[OSD([sQuery(id+"F0.wireOp",EDGE,"E0.left")])]}),makeQuery(id+"F3.opExtrude","SWEPT_FACE",FACE,{"disambiguationData":[OSD([sQuery(id+"F2.wireOp",EDGE,"E1.right")])]})]}),makeQuery(id+"F5.opExtrude","SWEPT_FACE",FACE,{"disambiguationData":[OSD([sQuery(id+"F4.wireOp",EDGE,"E2.right")])]})]}),makeQuery(id+"F9.opExtrude","SWEPT_FACE",FACE,{"disambiguationData":[OSD([sQuery(id+"F8.wireOp",EDGE,"E44")])]})]});
            var Q13;
            {var subQ0=sQuery(id+"F8.wireOp",EDGE,"E7");Q13=makeQuery(id+"F9.boolean.opBoolean","INTERSECT",EDGE,{"derivedFrom":[makeQuery(id+"F5.boolean.opBoolean","MERGE",FACE,{"derivedFrom":[makeQuery(id+"F3.boolean.opBoolean","MERGE",FACE,{"derivedFrom":[makeQuery(id+"F1.opExtrude","SWEPT_FACE",FACE,{"disambiguationData":[OSD([sQuery(id+"F0.wireOp",EDGE,"E0.left")])]}),makeQuery(id+"F3.opExtrude","SWEPT_FACE",FACE,{"disambiguationData":[OSD([sQuery(id+"F2.wireOp",EDGE,"E1.right")])]})]}),makeQuery(id+"F5.opExtrude","SWEPT_FACE",FACE,{"disambiguationData":[OSD([sQuery(id+"F4.wireOp",EDGE,"E2.right")])]})]}),makeQuery(id+"F9.opExtrude","SWEPT_FACE",FACE,{"disambiguationData":[OSD([subQ0]),TDD([makeQuery(id+"F8.imprint","IMPRINT",EDGE,{"disambiguationData":[TD([[makeQuery(id+"F8.imprint","INTERSECT",VERTEX,{"derivedFrom":[subQ0,sQuery(id+"F8.wireOp",EDGE,"E44")]}),-1.0]])],"derivedFrom":subQ0})])]})]});}
            var Q14;
            Q14=makeQuery(id+"F9.boolean.opBoolean","INTERSECT",EDGE,{"derivedFrom":[makeQuery(id+"F5.boolean.opBoolean","MERGE",FACE,{"derivedFrom":[makeQuery(id+"F3.boolean.opBoolean","MERGE",FACE,{"derivedFrom":[makeQuery(id+"F1.opExtrude","SWEPT_FACE",FACE,{"disambiguationData":[OSD([sQuery(id+"F0.wireOp",EDGE,"E0.left")])]}),makeQuery(id+"F3.opExtrude","SWEPT_FACE",FACE,{"disambiguationData":[OSD([sQuery(id+"F2.wireOp",EDGE,"E1.right")])]})]}),makeQuery(id+"F5.opExtrude","SWEPT_FACE",FACE,{"disambiguationData":[OSD([sQuery(id+"F4.wireOp",EDGE,"E2.right")])]})]}),makeQuery(id+"F9.opExtrude","SWEPT_FACE",FACE,{"disambiguationData":[OSD([sQuery(id+"F8.wireOp",EDGE,"E61")])]})]});
            var Q15;
            Q15=makeQuery(id+"F9.boolean.opBoolean","INTERSECT",EDGE,{"derivedFrom":[makeQuery(id+"F5.boolean.opBoolean","MERGE",FACE,{"derivedFrom":[makeQuery(id+"F3.boolean.opBoolean","MERGE",FACE,{"derivedFrom":[makeQuery(id+"F1.opExtrude","SWEPT_FACE",FACE,{"disambiguationData":[OSD([sQuery(id+"F0.wireOp",EDGE,"E0.left")])]}),makeQuery(id+"F3.opExtrude","SWEPT_FACE",FACE,{"disambiguationData":[OSD([sQuery(id+"F2.wireOp",EDGE,"E1.right")])]})]}),makeQuery(id+"F5.opExtrude","SWEPT_FACE",FACE,{"disambiguationData":[OSD([sQuery(id+"F4.wireOp",EDGE,"E2.right")])]})]}),makeQuery(id+"F9.opExtrude","SWEPT_FACE",FACE,{"disambiguationData":[OSD([sQuery(id+"F8.wireOp",EDGE,"E62")])]})]});
            var Q16;
            Q16=makeQuery(id+"F9.boolean.opBoolean","INTERSECT",EDGE,{"derivedFrom":[makeQuery(id+"F5.boolean.opBoolean","MERGE",FACE,{"derivedFrom":[makeQuery(id+"F3.boolean.opBoolean","MERGE",FACE,{"derivedFrom":[makeQuery(id+"F1.opExtrude","SWEPT_FACE",FACE,{"disambiguationData":[OSD([sQuery(id+"F0.wireOp",EDGE,"E0.left")])]}),makeQuery(id+"F3.opExtrude","SWEPT_FACE",FACE,{"disambiguationData":[OSD([sQuery(id+"F2.wireOp",EDGE,"E1.right")])]})]}),makeQuery(id+"F5.opExtrude","SWEPT_FACE",FACE,{"disambiguationData":[OSD([sQuery(id+"F4.wireOp",EDGE,"E2.right")])]})]}),makeQuery(id+"F9.opExtrude","SWEPT_FACE",FACE,{"disambiguationData":[OSD([sQuery(id+"F8.wireOp",EDGE,"E38")])]})]});
            var Q17;
            Q17=makeQuery(id+"F9.boolean.opBoolean","INTERSECT",EDGE,{"derivedFrom":[makeQuery(id+"F5.boolean.opBoolean","MERGE",FACE,{"derivedFrom":[makeQuery(id+"F3.boolean.opBoolean","MERGE",FACE,{"derivedFrom":[makeQuery(id+"F1.opExtrude","SWEPT_FACE",FACE,{"disambiguationData":[OSD([sQuery(id+"F0.wireOp",EDGE,"E0.left")])]}),makeQuery(id+"F3.opExtrude","SWEPT_FACE",FACE,{"disambiguationData":[OSD([sQuery(id+"F2.wireOp",EDGE,"E1.right")])]})]}),makeQuery(id+"F5.opExtrude","SWEPT_FACE",FACE,{"disambiguationData":[OSD([sQuery(id+"F4.wireOp",EDGE,"E2.right")])]})]}),makeQuery(id+"F9.opExtrude","SWEPT_FACE",FACE,{"disambiguationData":[OSD([sQuery(id+"F8.wireOp",EDGE,"E46")])]})]});
            var Q18;
            Q18=makeQuery(id+"F9.boolean.opBoolean","INTERSECT",EDGE,{"derivedFrom":[makeQuery(id+"F5.boolean.opBoolean","MERGE",FACE,{"derivedFrom":[makeQuery(id+"F3.boolean.opBoolean","MERGE",FACE,{"derivedFrom":[makeQuery(id+"F1.opExtrude","SWEPT_FACE",FACE,{"disambiguationData":[OSD([sQuery(id+"F0.wireOp",EDGE,"E0.left")])]}),makeQuery(id+"F3.opExtrude","SWEPT_FACE",FACE,{"disambiguationData":[OSD([sQuery(id+"F2.wireOp",EDGE,"E1.right")])]})]}),makeQuery(id+"F5.opExtrude","SWEPT_FACE",FACE,{"disambiguationData":[OSD([sQuery(id+"F4.wireOp",EDGE,"E2.right")])]})]}),makeQuery(id+"F9.opExtrude","SWEPT_FACE",FACE,{"disambiguationData":[OSD([sQuery(id+"F8.wireOp",EDGE,"E45")])]})]});
            var Q19;
            Q19=makeQuery(id+"F9.boolean.opBoolean","INTERSECT",EDGE,{"derivedFrom":[makeQuery(id+"F5.boolean.opBoolean","MERGE",FACE,{"derivedFrom":[makeQuery(id+"F3.boolean.opBoolean","MERGE",FACE,{"derivedFrom":[makeQuery(id+"F1.opExtrude","SWEPT_FACE",FACE,{"disambiguationData":[OSD([sQuery(id+"F0.wireOp",EDGE,"E0.left")])]}),makeQuery(id+"F3.opExtrude","SWEPT_FACE",FACE,{"disambiguationData":[OSD([sQuery(id+"F2.wireOp",EDGE,"E1.right")])]})]}),makeQuery(id+"F5.opExtrude","SWEPT_FACE",FACE,{"disambiguationData":[OSD([sQuery(id+"F4.wireOp",EDGE,"E2.right")])]})]}),makeQuery(id+"F9.opExtrude","SWEPT_FACE",FACE,{"disambiguationData":[OSD([sQuery(id+"F8.wireOp",EDGE,"E63")])]})]});
            var Q20;
            {var subQ0=sQuery(id+"F8.wireOp",EDGE,"E7");Q20=makeQuery(id+"F9.boolean.opBoolean","INTERSECT",EDGE,{"derivedFrom":[makeQuery(id+"F5.boolean.opBoolean","MERGE",FACE,{"derivedFrom":[makeQuery(id+"F3.boolean.opBoolean","MERGE",FACE,{"derivedFrom":[makeQuery(id+"F1.opExtrude","SWEPT_FACE",FACE,{"disambiguationData":[OSD([sQuery(id+"F0.wireOp",EDGE,"E0.left")])]}),makeQuery(id+"F3.opExtrude","SWEPT_FACE",FACE,{"disambiguationData":[OSD([sQuery(id+"F2.wireOp",EDGE,"E1.right")])]})]}),makeQuery(id+"F5.opExtrude","SWEPT_FACE",FACE,{"disambiguationData":[OSD([sQuery(id+"F4.wireOp",EDGE,"E2.right")])]})]}),makeQuery(id+"F9.opExtrude","SWEPT_FACE",FACE,{"disambiguationData":[OSD([subQ0]),TDD([makeQuery(id+"F8.imprint","IMPRINT",EDGE,{"disambiguationData":[TD([[makeQuery(id+"F8.imprint","INTERSECT",VERTEX,{"derivedFrom":[subQ0,sQuery(id+"F8.wireOp",EDGE,"E46")]}),-1.0]])],"derivedFrom":subQ0})])]})]});}
            var Q21;
            Q21=makeQuery(id+"F9.boolean.opBoolean","INTERSECT",EDGE,{"derivedFrom":[makeQuery(id+"F5.boolean.opBoolean","MERGE",FACE,{"derivedFrom":[makeQuery(id+"F3.boolean.opBoolean","MERGE",FACE,{"derivedFrom":[makeQuery(id+"F1.opExtrude","SWEPT_FACE",FACE,{"disambiguationData":[OSD([sQuery(id+"F0.wireOp",EDGE,"E0.left")])]}),makeQuery(id+"F3.opExtrude","SWEPT_FACE",FACE,{"disambiguationData":[OSD([sQuery(id+"F2.wireOp",EDGE,"E1.right")])]})]}),makeQuery(id+"F5.opExtrude","SWEPT_FACE",FACE,{"disambiguationData":[OSD([sQuery(id+"F4.wireOp",EDGE,"E2.right")])]})]}),makeQuery(id+"F9.opExtrude","SWEPT_FACE",FACE,{"disambiguationData":[OSD([sQuery(id+"F8.wireOp",EDGE,"E64")])]})]});
            var Q22;
            Q22=makeQuery(id+"F9.boolean.opBoolean","INTERSECT",EDGE,{"derivedFrom":[makeQuery(id+"F5.boolean.opBoolean","MERGE",FACE,{"derivedFrom":[makeQuery(id+"F3.boolean.opBoolean","MERGE",FACE,{"derivedFrom":[makeQuery(id+"F1.opExtrude","SWEPT_FACE",FACE,{"disambiguationData":[OSD([sQuery(id+"F0.wireOp",EDGE,"E0.left")])]}),makeQuery(id+"F3.opExtrude","SWEPT_FACE",FACE,{"disambiguationData":[OSD([sQuery(id+"F2.wireOp",EDGE,"E1.right")])]})]}),makeQuery(id+"F5.opExtrude","SWEPT_FACE",FACE,{"disambiguationData":[OSD([sQuery(id+"F4.wireOp",EDGE,"E2.right")])]})]}),makeQuery(id+"F9.opExtrude","SWEPT_FACE",FACE,{"disambiguationData":[OSD([sQuery(id+"F8.wireOp",EDGE,"E39")])]})]});
            var Q23;
            Q23=makeQuery(id+"F9.boolean.opBoolean","INTERSECT",EDGE,{"derivedFrom":[makeQuery(id+"F5.boolean.opBoolean","MERGE",FACE,{"derivedFrom":[makeQuery(id+"F3.boolean.opBoolean","MERGE",FACE,{"derivedFrom":[makeQuery(id+"F1.opExtrude","SWEPT_FACE",FACE,{"disambiguationData":[OSD([sQuery(id+"F0.wireOp",EDGE,"E0.left")])]}),makeQuery(id+"F3.opExtrude","SWEPT_FACE",FACE,{"disambiguationData":[OSD([sQuery(id+"F2.wireOp",EDGE,"E1.right")])]})]}),makeQuery(id+"F5.opExtrude","SWEPT_FACE",FACE,{"disambiguationData":[OSD([sQuery(id+"F4.wireOp",EDGE,"E2.right")])]})]}),makeQuery(id+"F9.opExtrude","SWEPT_FACE",FACE,{"disambiguationData":[OSD([sQuery(id+"F8.wireOp",EDGE,"E40")])]})]});
            var Q24;
            {var subQ0=sQuery(id+"F2.wireOp",EDGE,"E1.right");var subQ1=makeQuery(id+"F3.opExtrude","SWEPT_FACE",FACE,{"disambiguationData":[OSD([subQ0])]});var subQ2=sQuery(id+"F0.wireOp",EDGE,"E0.left");var subQ3=makeQuery(id+"F1.opExtrude","SWEPT_FACE",FACE,{"disambiguationData":[OSD([subQ2])]});var subQ4=sQuery(id+"F2.wireOp",EDGE,"E1.bottom");Q24=makeQuery(id+"F10.opFillet","BLEND_EDGE",EDGE,{"blendedFrom":[makeQuery(id+"F3.boolean.opBoolean","SPLIT",EDGE,{"disambiguationData":[TD([makeQuery(id+"F3.opExtrude","SWEPT_FACE",FACE,{"disambiguationData":[OSD([subQ4])]})])],"derivedFrom":makeQuery(id+"F3.opExtrude","CAP_EDGE",EDGE,{"disambiguationData":[OSD([subQ0])],"isStart":true})}),makeQuery(id+"F5.boolean.opBoolean","MERGE",FACE,{"derivedFrom":[makeQuery(id+"F3.boolean.opBoolean","MERGE",FACE,{"derivedFrom":[subQ3,subQ1]}),makeQuery(id+"F5.opExtrude","SWEPT_FACE",FACE,{"disambiguationData":[OSD([sQuery(id+"F4.wireOp",EDGE,"E2.right")])]})]})],"blendedInto":[makeQuery(id+"F5.boolean.opBoolean","MERGE",FACE,{"derivedFrom":[makeQuery(id+"F3.boolean.opBoolean","MERGE",FACE,{"derivedFrom":[subQ3,subQ1]}),makeQuery(id+"F5.opExtrude","SWEPT_FACE",FACE,{"disambiguationData":[OSD([sQuery(id+"F4.wireOp",EDGE,"E2.right")])]})]})]});}
            var Q25;
            {var subQ0=sQuery(id+"F2.wireOp",EDGE,"E1.right");Q25=makeQuery(id+"F10.opFillet","BLEND_EDGE",EDGE,{"blendedFrom":[makeQuery(id+"F3.opExtrude","CAP_EDGE",EDGE,{"disambiguationData":[OSD([subQ0])],"isStart":false}),makeQuery(id+"F3.opExtrude","CAP_FACE",FACE,{"disambiguationData":[OSD([sQuery(id+"F2.wireOp",EDGE,"E1.bottom"),sQuery(id+"F2.wireOp",EDGE,"E1.top"),sQuery(id+"F2.wireOp",EDGE,"E1.left"),subQ0])],"isStart":false})],"blendedInto":[makeQuery(id+"F3.opExtrude","CAP_FACE",FACE,{"disambiguationData":[OSD([sQuery(id+"F2.wireOp",EDGE,"E1.bottom"),sQuery(id+"F2.wireOp",EDGE,"E1.top"),sQuery(id+"F2.wireOp",EDGE,"E1.left"),subQ0])],"isStart":false})]});}
            var Q26;
            {var subQ0=sQuery(id+"F2.wireOp",EDGE,"E1.left");var subQ1=sQuery(id+"F2.wireOp",EDGE,"E1.top");Q26=makeQuery(id+"F10.opFillet","BLEND_EDGE",EDGE,{"blendedFrom":[makeQuery(id+"F7.boolean.opBoolean","MERGE",EDGE,{"derivedFrom":[makeQuery(id+"F3.opExtrude","CAP_EDGE",EDGE,{"disambiguationData":[OSD([subQ1])],"isStart":false}),makeQuery(id+"F7.opExtrude","SWEPT_EDGE",EDGE,{"disambiguationData":[OSD([subQ1,subQ0,sQuery(id+"F4.wireOp",EDGE,"E2.left"),sQuery(id+"F6.wireOp",EDGE,"E6")])]})]}),makeQuery(id+"F3.opExtrude","CAP_FACE",FACE,{"disambiguationData":[OSD([sQuery(id+"F2.wireOp",EDGE,"E1.bottom"),subQ1,subQ0,sQuery(id+"F2.wireOp",EDGE,"E1.right")])],"isStart":false})],"blendedInto":[makeQuery(id+"F3.opExtrude","CAP_FACE",FACE,{"disambiguationData":[OSD([sQuery(id+"F2.wireOp",EDGE,"E1.bottom"),subQ1,subQ0,sQuery(id+"F2.wireOp",EDGE,"E1.right")])],"isStart":false})]});}
            var Q27;
            {var subQ0=sQuery(id+"F2.wireOp",EDGE,"E1.bottom");Q27=makeQuery(id+"F10.opFillet","BLEND_EDGE",EDGE,{"blendedFrom":[makeQuery(id+"F3.opExtrude","CAP_EDGE",EDGE,{"disambiguationData":[OSD([subQ0])],"isStart":false}),makeQuery(id+"F3.opExtrude","CAP_FACE",FACE,{"disambiguationData":[OSD([subQ0,sQuery(id+"F2.wireOp",EDGE,"E1.top"),sQuery(id+"F2.wireOp",EDGE,"E1.left"),sQuery(id+"F2.wireOp",EDGE,"E1.right")])],"isStart":false})],"blendedInto":[makeQuery(id+"F3.opExtrude","CAP_FACE",FACE,{"disambiguationData":[OSD([subQ0,sQuery(id+"F2.wireOp",EDGE,"E1.top"),sQuery(id+"F2.wireOp",EDGE,"E1.left"),sQuery(id+"F2.wireOp",EDGE,"E1.right")])],"isStart":false})]});}
            var Q28;
            Q28=makeQuery(id+"F3.opExtrude","SWEPT_EDGE",EDGE,{"disambiguationData":[OSD([sQuery(id+"F2.wireOp",EDGE,"E1.bottom"),sQuery(id+"F2.wireOp",EDGE,"E1.right")])]});
            fillet(context, id + "F12", {"entities" : qUnion([Q0, Q1, Q2, Q3, Q4, Q5, Q6, Q7, Q8, Q9, Q10, Q11, Q12, Q13, Q14, Q15, Q16, Q17, Q18, Q19, Q20, Q21, Q22, Q23, Q24, Q25, Q26, Q27, Q28]), "radius" : 0.05 * mm, "tangentPropagation" : true, "allowEdgeOverflow" : false});
        }
        {
            var Q0;
            Q0=makeQuery(id+"F9.boolean.opBoolean","COPY",FACE,{"derivedFrom":makeQuery(id+"F9.opExtrude","SWEPT_FACE",FACE,{"disambiguationData":[OSD([sQuery(id+"F8.wireOp",EDGE,"E35")])]})});
            var Q1;
            Q1=makeQuery(id+"F9.boolean.opBoolean","COPY",FACE,{"derivedFrom":makeQuery(id+"F9.opExtrude","SWEPT_FACE",FACE,{"disambiguationData":[OSD([sQuery(id+"F8.wireOp",EDGE,"E42")])]})});
            var Q2;
            Q2=makeQuery(id+"F9.boolean.opBoolean","COPY",FACE,{"derivedFrom":makeQuery(id+"F9.opExtrude","SWEPT_FACE",FACE,{"disambiguationData":[OSD([sQuery(id+"F8.wireOp",EDGE,"E44")])]})});
            var Q3;
            Q3=makeQuery(id+"F9.boolean.opBoolean","COPY",FACE,{"derivedFrom":makeQuery(id+"F9.opExtrude","SWEPT_FACE",FACE,{"disambiguationData":[OSD([sQuery(id+"F8.wireOp",EDGE,"E46")])]})});
            var Q4;
            Q4=makeQuery(id+"F3.opExtrude","CAP_FACE",FACE,{"disambiguationData":[OSD([sQuery(id+"F2.wireOp",EDGE,"E1.bottom"),sQuery(id+"F2.wireOp",EDGE,"E1.top"),sQuery(id+"F2.wireOp",EDGE,"E1.left"),sQuery(id+"F2.wireOp",EDGE,"E1.right")])],"isStart":false});
            fillet(context, id + "F13", {"entities" : qUnion([Q0, Q1, Q2, Q3, Q4]), "radius" : 0.05 * mm, "tangentPropagation" : true, "allowEdgeOverflow" : false});
        }
        {
            var Q0;
            Q0=makeQuery(id+"F5.boolean.opBoolean","MERGE",FACE,{"derivedFrom":[makeQuery(id+"F1.opExtrude","SWEPT_FACE",FACE,{"disambiguationData":[OSD([sQuery(id+"F0.wireOp",EDGE,"E0.bottom")])]}),makeQuery(id+"F5.opExtrude","SWEPT_FACE",FACE,{"disambiguationData":[OSD([sQuery(id+"F4.wireOp",EDGE,"E2.top")])]})]});
            var Q1;
            Q1=makeQuery(id+"F9.boolean.opBoolean","COPY",FACE,{"derivedFrom":makeQuery(id+"F9.opExtrude","SWEPT_FACE",FACE,{"disambiguationData":[OSD([sQuery(id+"F8.wireOp",EDGE,"E41")])]})});
            var Q2;
            Q2=makeQuery(id+"F9.boolean.opBoolean","COPY",FACE,{"derivedFrom":makeQuery(id+"F9.opExtrude","SWEPT_FACE",FACE,{"disambiguationData":[OSD([sQuery(id+"F8.wireOp",EDGE,"E43")])]})});
            var Q3;
            Q3=makeQuery(id+"F9.boolean.opBoolean","COPY",FACE,{"derivedFrom":makeQuery(id+"F9.opExtrude","SWEPT_FACE",FACE,{"disambiguationData":[OSD([sQuery(id+"F8.wireOp",EDGE,"E45")])]})});
            var Q4;
            Q4=makeQuery(id+"F9.boolean.opBoolean","COPY",FACE,{"derivedFrom":makeQuery(id+"F9.opExtrude","SWEPT_FACE",FACE,{"disambiguationData":[OSD([sQuery(id+"F8.wireOp",EDGE,"E40")])]})});
            var Q5;
            {var subQ0=sQuery(id+"F2.wireOp",EDGE,"E1.bottom");var subQ2=sQuery(id+"F2.wireOp",EDGE,"E1.left");var subQ4=sQuery(id+"F2.wireOp",EDGE,"E1.right");Q5=makeQuery(id+"F3.boolean.opBoolean","SPLIT",FACE,{"disambiguationData":[TD([makeQuery(id+"F3.opExtrude","SWEPT_FACE",FACE,{"disambiguationData":[OSD([subQ0])]})])],"derivedFrom":makeQuery(id+"F3.opExtrude","CAP_FACE",FACE,{"disambiguationData":[OSD([subQ0,sQuery(id+"F2.wireOp",EDGE,"E1.top"),subQ2,subQ4])],"isStart":true})});}
            fillet(context, id + "F14", {"entities" : qUnion([Q0, Q1, Q2, Q3, Q4, Q5]), "radius" : 0.05 * mm, "tangentPropagation" : true, "allowEdgeOverflow" : false});
        }
        {
            var Q0;
            Q0=makeQuery(id+"F3.opExtrude","CAP_FACE",FACE,{"disambiguationData":[OSD([sQuery(id+"F2.wireOp",EDGE,"E1.bottom"),sQuery(id+"F2.wireOp",EDGE,"E1.top"),sQuery(id+"F2.wireOp",EDGE,"E1.left"),sQuery(id+"F2.wireOp",EDGE,"E1.right")])],"isStart":false});
            var sketch = newSketch(context, id + "F15", { "sketchPlane" : qUnion([Q0])});
            skLineSegment(sketch, "E65.bottom", {"start": v(42.5, 42.5) * mm, "end": v(-42.5, 42.5) * mm});
            skLineSegment(sketch, "E65.top", {"start": v(42.5, -42.5) * mm, "end": v(-42.5, -42.5) * mm});
            skLineSegment(sketch, "E65.left", {"start": v(42.5, 42.5) * mm, "end": v(42.5, -42.5) * mm});
            skLineSegment(sketch, "E65.right", {"start": v(-42.5, 42.5) * mm, "end": v(-42.5, -42.5) * mm});
            skPoint(sketch, "E65.middle", {"position": v(0, 0) * mm});
            skSolve(sketch);
        }
        {
            var Q0;
            Q0 = qSketchRegion(id + "F15", true);
            extrude(context, id + "F16", {"entities" : qUnion([Q0]), "operationType" : NewBodyOperationType.ADD, "depth" : 3 * mm, "offsetDistance" : 25 * mm});
        }
        {
            var Q0;
            Q0=makeQuery(id+"F16.opExtrude","CAP_FACE",FACE,{"disambiguationData":[OSD([sQuery(id+"F15.wireOp",EDGE,"E65.bottom"),sQuery(id+"F15.wireOp",EDGE,"E65.top"),sQuery(id+"F15.wireOp",EDGE,"E65.left"),sQuery(id+"F15.wireOp",EDGE,"E65.right")])],"isStart":false});
            var sketch = newSketch(context, id + "F17", { "sketchPlane" : qUnion([Q0])});
            skPoint(sketch, "E66", {"position": v(37.5, 37.5) * mm});
            skPoint(sketch, "E67", {"position": v(37.5, -37.5) * mm});
            skPoint(sketch, "E68", {"position": v(-37.5, 37.5) * mm});
            skPoint(sketch, "E69", {"position": v(-37.5, -37.5) * mm});
            skCircle(sketch, "E70", {"center": v(-37.5, 37.5) * mm, "radius": 1.5 * mm});
            skCircle(sketch, "E71", {"center": v(37.5, 37.5) * mm, "radius": 1.5 * mm});
            skCircle(sketch, "E72", {"center": v(37.5, -37.5) * mm, "radius": 1.5 * mm});
            skCircle(sketch, "E73", {"center": v(-37.5, -37.5) * mm, "radius": 1.5 * mm});
            skSolve(sketch);
        }
        {
            var Q0;
            Q0=makeQuery(id+"F17.imprint","IMPRINT",FACE,{"disambiguationData":[TD([[makeQuery(id+"F17.imprint","IMPRINT",EDGE,{"derivedFrom":sQuery(id+"F17.wireOp",EDGE,"E70")}),1.0]])]});
            var Q1;
            Q1=makeQuery(id+"F17.imprint","IMPRINT",FACE,{"disambiguationData":[TD([[makeQuery(id+"F17.imprint","IMPRINT",EDGE,{"derivedFrom":sQuery(id+"F17.wireOp",EDGE,"E71")}),1.0]])]});
            var Q2;
            Q2=makeQuery(id+"F17.imprint","IMPRINT",FACE,{"disambiguationData":[TD([[makeQuery(id+"F17.imprint","IMPRINT",EDGE,{"derivedFrom":sQuery(id+"F17.wireOp",EDGE,"E72")}),1.0]])]});
            var Q3;
            Q3=makeQuery(id+"F17.imprint","IMPRINT",FACE,{"disambiguationData":[TD([[makeQuery(id+"F17.imprint","IMPRINT",EDGE,{"derivedFrom":sQuery(id+"F17.wireOp",EDGE,"E73")}),1.0]])]});
            extrude(context, id + "F18", {"entities" : qUnion([Q0, Q1, Q2, Q3]), "operationType" : NewBodyOperationType.REMOVE, "oppositeDirection" : true, "depth" : 25 * mm, "offsetDistance" : 25 * mm});
        }
    });
